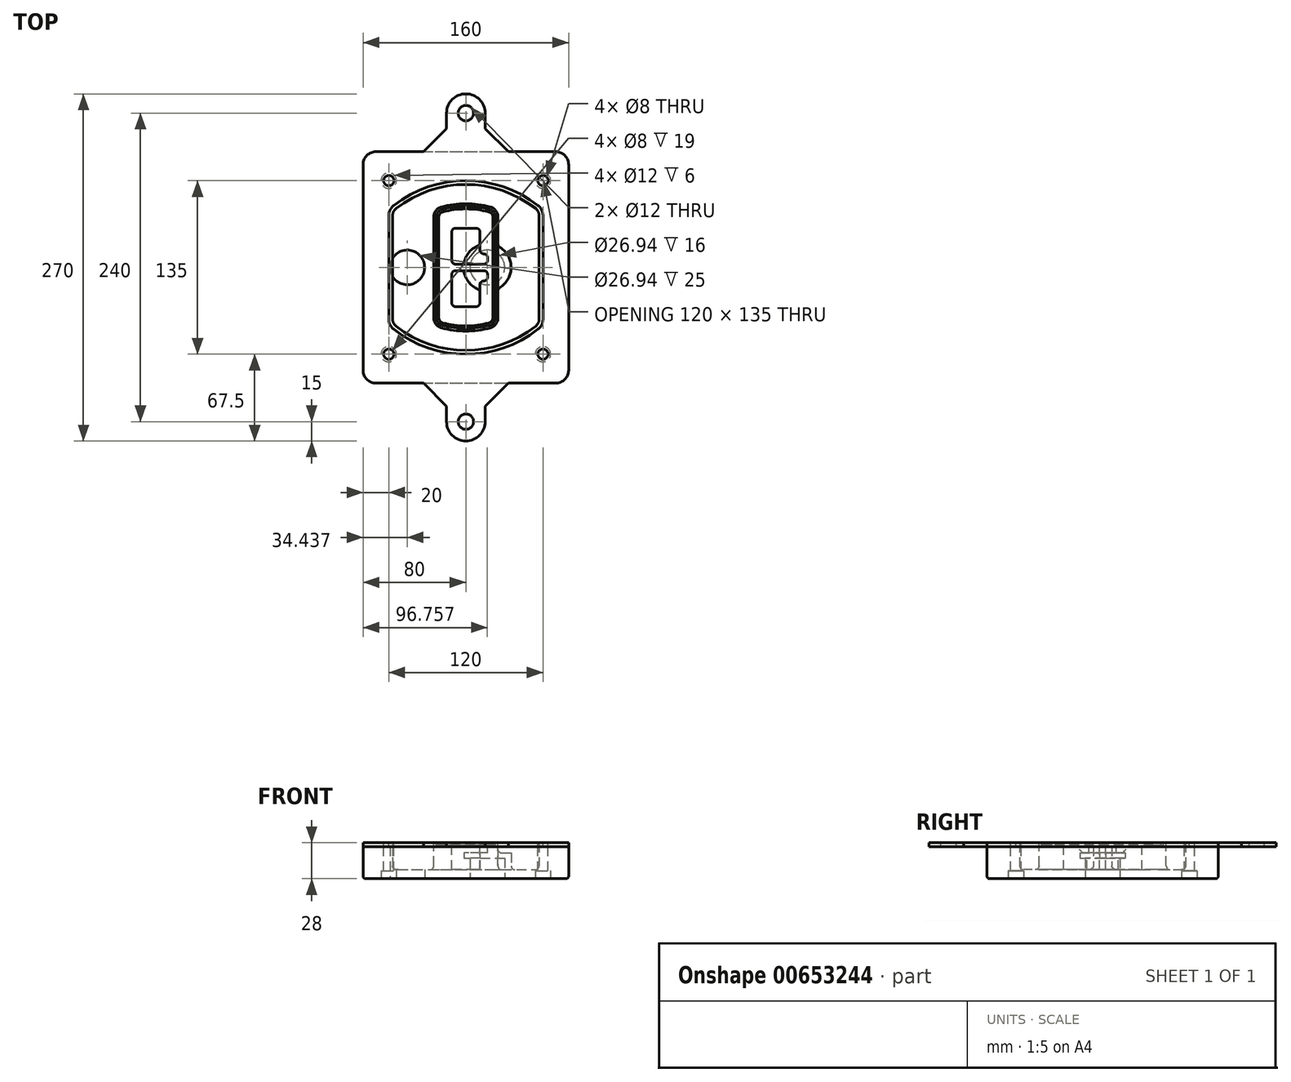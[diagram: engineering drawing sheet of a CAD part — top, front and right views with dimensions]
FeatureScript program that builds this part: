
annotation { "Feature Type Name" : "Feature", "Feature Type Description" : "" }
export const myFeature = defineFeature(function(context is Context, id is Id, definition is map)
    precondition{}
    {
        {
            var Q0;
            Q0=qCreatedBy(makeId("Top.planeOp"),FACE);
            var sketch = newSketch(context, id + "F0", { "sketchPlane" : qUnion([Q0])});
            skPoint(sketch, "E0.rect.middle", {"position": v(0, 0) * mm});
            skLineSegment(sketch, "E1.bottom", {"start": v(-70, -90) * mm, "end": v(70, -90) * mm});
            skLineSegment(sketch, "E1.top", {"start": v(-70, 90) * mm, "end": v(70, 90) * mm});
            skLineSegment(sketch, "E1.left", {"start": v(-80, -80) * mm, "end": v(-80, 80) * mm});
            skLineSegment(sketch, "E1.right", {"start": v(80, -80) * mm, "end": v(80, 80) * mm});
            skLineSegment(sketch, "E2", {"start": v(-80, 90) * mm, "end": v(80, -90) * mm, "construction": true});
            skLineSegment(sketch, "E3", {"start": v(80, 90) * mm, "end": v(-80, -90) * mm, "construction": true});
            skCircle(sketch, "E4", {"center": v(-60, 67.5) * mm, "radius": 4 * mm});
            skCircle(sketch, "E5", {"center": v(60, 67.5) * mm, "radius": 4 * mm});
            skCircle(sketch, "E6", {"center": v(60, -67.5) * mm, "radius": 4 * mm});
            skCircle(sketch, "E7", {"center": v(-60, -67.5) * mm, "radius": 4 * mm});
            skLineSegment(sketch, "E8", {"start": v(-60, 67.5) * mm, "end": v(60, 67.5) * mm, "construction": true});
            skLineSegment(sketch, "E9", {"start": v(60, 67.5) * mm, "end": v(60, -67.5) * mm, "construction": true});
            skLineSegment(sketch, "E10", {"start": v(60, -67.5) * mm, "end": v(-60, -67.5) * mm, "construction": true});
            skLineSegment(sketch, "E11", {"start": v(-60, -67.5) * mm, "end": v(-60, 67.5) * mm, "construction": true});
            skLineSegment(sketch, "E12", {"start": v(-60, 40.3) * mm, "end": v(-60, -40.3) * mm});
            skLineSegment(sketch, "E13", {"start": v(60, 40.3) * mm, "end": v(60, -40.3) * mm});
            skArc(sketch, "E14", {"start": v(56.15, 48.18) * mm, "mid": v(0, 67.5) * mm, "end": v(-56.15, 48.18) * mm});
            skArc(sketch, "E15", {"start": v(-56.15, -48.18) * mm, "mid": v(0, -67.5) * mm, "end": v(56.15, -48.18) * mm});
            skLineSegment(sketch, "E16", {"start": v(-60, 0) * mm, "end": v(60, 0) * mm, "construction": true});
            skPoint(sketch, "E17.visualSharp", {"position": v(-60, -45) * mm});
            skArc(sketch, "E17.filletArc", {"start": v(-60, -40.3) * mm, "mid": v(-58.99, -44.68) * mm, "end": v(-56.15, -48.18) * mm});
            skPoint(sketch, "E18.visualSharp", {"position": v(-60, 45) * mm});
            skArc(sketch, "E18.filletArc", {"start": v(-56.15, 48.18) * mm, "mid": v(-58.99, 44.68) * mm, "end": v(-60, 40.3) * mm});
            skPoint(sketch, "E19.visualSharp", {"position": v(60, 45) * mm});
            skArc(sketch, "E19.filletArc", {"start": v(60, 40.3) * mm, "mid": v(58.99, 44.68) * mm, "end": v(56.15, 48.18) * mm});
            skPoint(sketch, "E20.visualSharp", {"position": v(60, -45) * mm});
            skArc(sketch, "E20.filletArc", {"start": v(56.15, -48.18) * mm, "mid": v(58.99, -44.68) * mm, "end": v(60, -40.3) * mm});
            skPoint(sketch, "E21.visualSharp", {"position": v(-80, 90) * mm});
            skArc(sketch, "E21.filletArc", {"start": v(-70, 90) * mm, "mid": v(-77.07, 87.07) * mm, "end": v(-80, 80) * mm});
            skPoint(sketch, "E22.visualSharp", {"position": v(80, 90) * mm});
            skArc(sketch, "E22.filletArc", {"start": v(80, 80) * mm, "mid": v(77.07, 87.07) * mm, "end": v(70, 90) * mm});
            skPoint(sketch, "E23.visualSharp", {"position": v(80, -90) * mm});
            skArc(sketch, "E23.filletArc", {"start": v(70, -90) * mm, "mid": v(77.07, -87.07) * mm, "end": v(80, -80) * mm});
            skPoint(sketch, "E24.visualSharp", {"position": v(-80, -90) * mm});
            skArc(sketch, "E24.filletArc", {"start": v(-80, -80) * mm, "mid": v(-77.07, -87.07) * mm, "end": v(-70, -90) * mm});
            skArc(sketch, "E25.0", {"start": v(57, 40.3) * mm, "mid": v(56.3, 43.36) * mm, "end": v(54.3, 45.81) * mm});
            skLineSegment(sketch, "E25.1", {"start": v(57, 40.3) * mm, "end": v(57, -40.3) * mm});
            skArc(sketch, "E25.2", {"start": v(54.3, -45.81) * mm, "mid": v(56.3, -43.36) * mm, "end": v(57, -40.3) * mm});
            skArc(sketch, "E25.3", {"start": v(-54.3, -45.81) * mm, "mid": v(0, -64.5) * mm, "end": v(54.3, -45.81) * mm});
            skArc(sketch, "E25.4", {"start": v(-57, -40.3) * mm, "mid": v(-56.3, -43.36) * mm, "end": v(-54.3, -45.81) * mm});
            skArc(sketch, "E25.5", {"start": v(54.3, 45.81) * mm, "mid": v(0, 64.5) * mm, "end": v(-54.3, 45.81) * mm});
            skLineSegment(sketch, "E25.6", {"start": v(-57, 40.3) * mm, "end": v(-57, -40.3) * mm});
            skArc(sketch, "E25.7", {"start": v(-54.3, 45.81) * mm, "mid": v(-56.3, 43.36) * mm, "end": v(-57, 40.3) * mm});
            skArc(sketch, "E26.0", {"start": v(-58.62, 51.33) * mm, "mid": v(-62.58, 46.43) * mm, "end": v(-64, 40.3) * mm});
            skArc(sketch, "E26.1", {"start": v(58.62, 51.33) * mm, "mid": v(0, 71.5) * mm, "end": v(-58.62, 51.33) * mm});
            skArc(sketch, "E26.2", {"start": v(64, 40.3) * mm, "mid": v(62.58, 46.43) * mm, "end": v(58.62, 51.33) * mm});
            skLineSegment(sketch, "E26.3", {"start": v(64, 40.3) * mm, "end": v(64, -40.3) * mm});
            skArc(sketch, "E26.4", {"start": v(58.62, -51.33) * mm, "mid": v(62.58, -46.43) * mm, "end": v(64, -40.3) * mm});
            skLineSegment(sketch, "E26.5", {"start": v(-64, 40.3) * mm, "end": v(-64, -40.3) * mm});
            skArc(sketch, "E26.6", {"start": v(-58.62, -51.33) * mm, "mid": v(0, -71.5) * mm, "end": v(58.62, -51.33) * mm});
            skArc(sketch, "E26.7", {"start": v(-64, -40.3) * mm, "mid": v(-62.58, -46.43) * mm, "end": v(-58.62, -51.33) * mm});
            skSolve(sketch);
        }
        {
            var Q0;
            Q0=makeQuery(id+"F0.imprint","IMPRINT",FACE,{"disambiguationData":[TD([[makeQuery(id+"F0.imprint","IMPRINT",EDGE,{"derivedFrom":sQuery(id+"F0.wireOp",EDGE,"E1.bottom")}),1.0]])]});
            var Q1;
            Q1=makeQuery(id+"F0.imprint","IMPRINT",FACE,{"disambiguationData":[TD([[makeQuery(id+"F0.imprint","IMPRINT",EDGE,{"derivedFrom":sQuery(id+"F0.wireOp",EDGE,"E12")}),1.0]])]});
            var Q2;
            Q2=makeQuery(id+"F0.imprint","IMPRINT",FACE,{"disambiguationData":[TD([[makeQuery(id+"F0.imprint","IMPRINT",EDGE,{"derivedFrom":sQuery(id+"F0.wireOp",EDGE,"E25.0")}),1.0]])]});
            var Q3;
            Q3=makeQuery(id+"F0.imprint","IMPRINT",FACE,{"disambiguationData":[TD([[makeQuery(id+"F0.imprint","IMPRINT",EDGE,{"derivedFrom":sQuery(id+"F0.wireOp",EDGE,"E12")}),-1.0]])]});
            extrude(context, id + "F1", {"entities" : qUnion([Q0, Q1, Q2, Q3]), "oppositeDirection" : true, "depth" : 25 * mm});
        }
        {
            var Q0;
            Q0=makeQuery(id+"F0.imprint","IMPRINT",FACE,{"disambiguationData":[TD([[makeQuery(id+"F0.imprint","IMPRINT",EDGE,{"derivedFrom":sQuery(id+"F0.wireOp",EDGE,"E12")}),1.0]])]});
            extrude(context, id + "F2", {"entities" : qUnion([Q0]), "operationType" : NewBodyOperationType.ADD, "depth" : 3 * mm});
        }
        {
            var Q0;
            Q0=makeQuery(id+"F0.imprint","IMPRINT",FACE,{"disambiguationData":[TD([[makeQuery(id+"F0.imprint","IMPRINT",EDGE,{"derivedFrom":sQuery(id+"F0.wireOp",EDGE,"E25.0")}),1.0]])]});
            extrude(context, id + "F3", {"entities" : qUnion([Q0]), "operationType" : NewBodyOperationType.REMOVE, "oppositeDirection" : true, "depth" : 18 * mm});
        }
        {
            var Q0;
            Q0=makeQuery(id+"F2.opExtrude","CAP_FACE",FACE,{"disambiguationData":[OSD([sQuery(id+"F0.wireOp",EDGE,"E12"),sQuery(id+"F0.wireOp",EDGE,"E13"),sQuery(id+"F0.wireOp",EDGE,"E14"),sQuery(id+"F0.wireOp",EDGE,"E15"),sQuery(id+"F0.wireOp",EDGE,"E17.filletArc"),sQuery(id+"F0.wireOp",EDGE,"E18.filletArc"),sQuery(id+"F0.wireOp",EDGE,"E19.filletArc"),sQuery(id+"F0.wireOp",EDGE,"E20.filletArc"),sQuery(id+"F0.wireOp",EDGE,"E25.0"),sQuery(id+"F0.wireOp",EDGE,"E25.1"),sQuery(id+"F0.wireOp",EDGE,"E25.2"),sQuery(id+"F0.wireOp",EDGE,"E25.3"),sQuery(id+"F0.wireOp",EDGE,"E25.4"),sQuery(id+"F0.wireOp",EDGE,"E25.5"),sQuery(id+"F0.wireOp",EDGE,"E25.6"),sQuery(id+"F0.wireOp",EDGE,"E25.7")])],"isStart":false});
            var sketch = newSketch(context, id + "F4", { "sketchPlane" : qUnion([Q0])});
            skArc(sketch, "E27.0", {"start": v(-19.08, -46.97) * mm, "mid": v(0, -49.5) * mm, "end": v(19.08, -46.97) * mm});
            skArc(sketch, "E28.0", {"start": v(19.08, 46.97) * mm, "mid": v(0, 49.5) * mm, "end": v(-19.08, 46.97) * mm});
            skLineSegment(sketch, "E29", {"start": v(-25, 39.25) * mm, "end": v(-25, -39.25) * mm});
            skLineSegment(sketch, "E30", {"start": v(25, 39.25) * mm, "end": v(25, -39.25) * mm});
            skLineSegment(sketch, "E31", {"start": v(-25, 45.1) * mm, "end": v(25, 45.1) * mm, "construction": true});
            skLineSegment(sketch, "E32", {"start": v(-25, -45.1) * mm, "end": v(25, -45.1) * mm, "construction": true});
            skPoint(sketch, "E33.visualSharp", {"position": v(-25, 45.1) * mm});
            skArc(sketch, "E33.filletArc", {"start": v(-19.08, 46.97) * mm, "mid": v(-23.35, 44.11) * mm, "end": v(-25, 39.25) * mm});
            skPoint(sketch, "E34.visualSharp", {"position": v(25, 45.1) * mm});
            skArc(sketch, "E34.filletArc", {"start": v(25, 39.25) * mm, "mid": v(23.35, 44.11) * mm, "end": v(19.08, 46.97) * mm});
            skPoint(sketch, "E35.visualSharp", {"position": v(25, -45.1) * mm});
            skArc(sketch, "E35.filletArc", {"start": v(19.08, -46.97) * mm, "mid": v(23.35, -44.11) * mm, "end": v(25, -39.25) * mm});
            skPoint(sketch, "E36.visualSharp", {"position": v(-25, -45.1) * mm});
            skArc(sketch, "E36.filletArc", {"start": v(-25, -39.25) * mm, "mid": v(-23.35, -44.11) * mm, "end": v(-19.08, -46.97) * mm});
            skArc(sketch, "E37.0", {"start": v(54.3, 45.81) * mm, "mid": v(0, 64.5) * mm, "end": v(-54.3, 45.81) * mm});
            skArc(sketch, "E37.1", {"start": v(-54.3, 45.81) * mm, "mid": v(-56.3, 43.36) * mm, "end": v(-57, 40.3) * mm});
            skLineSegment(sketch, "E37.2", {"start": v(-57, 40.3) * mm, "end": v(-57, -40.3) * mm});
            skArc(sketch, "E37.3", {"start": v(-57, -40.3) * mm, "mid": v(-56.3, -43.36) * mm, "end": v(-54.3, -45.81) * mm});
            skArc(sketch, "E37.4", {"start": v(-54.3, -45.81) * mm, "mid": v(0, -64.5) * mm, "end": v(54.3, -45.81) * mm});
            skArc(sketch, "E37.5", {"start": v(54.3, -45.81) * mm, "mid": v(56.3, -43.36) * mm, "end": v(57, -40.3) * mm});
            skLineSegment(sketch, "E37.6", {"start": v(57, 40.3) * mm, "end": v(57, -40.3) * mm});
            skArc(sketch, "E37.7", {"start": v(57, 40.3) * mm, "mid": v(56.3, 43.36) * mm, "end": v(54.3, 45.81) * mm});
            skLineSegment(sketch, "E38.0", {"start": v(23, 39.25) * mm, "end": v(23, -39.25) * mm});
            skArc(sketch, "E38.1", {"start": v(18.56, -45.04) * mm, "mid": v(21.76, -42.9) * mm, "end": v(23, -39.25) * mm});
            skArc(sketch, "E38.2", {"start": v(-18.56, -45.04) * mm, "mid": v(0, -47.5) * mm, "end": v(18.56, -45.04) * mm});
            skArc(sketch, "E38.3", {"start": v(-23, -39.25) * mm, "mid": v(-21.76, -42.9) * mm, "end": v(-18.56, -45.04) * mm});
            skLineSegment(sketch, "E38.4", {"start": v(-23, 39.25) * mm, "end": v(-23, -39.25) * mm});
            skArc(sketch, "E38.5", {"start": v(23, 39.25) * mm, "mid": v(21.76, 42.9) * mm, "end": v(18.56, 45.04) * mm});
            skArc(sketch, "E38.6", {"start": v(-18.56, 45.04) * mm, "mid": v(-21.76, 42.9) * mm, "end": v(-23, 39.25) * mm});
            skArc(sketch, "E38.7", {"start": v(18.56, 45.04) * mm, "mid": v(0, 47.5) * mm, "end": v(-18.56, 45.04) * mm});
            skArc(sketch, "E39.0", {"start": v(21, 39.25) * mm, "mid": v(20.18, 41.68) * mm, "end": v(18.04, 43.1) * mm});
            skLineSegment(sketch, "E39.1", {"start": v(21, 39.25) * mm, "end": v(21, -39.25) * mm});
            skArc(sketch, "E39.2", {"start": v(18.04, -43.1) * mm, "mid": v(20.18, -41.68) * mm, "end": v(21, -39.25) * mm});
            skArc(sketch, "E39.3", {"start": v(-18.04, -43.1) * mm, "mid": v(0, -45.5) * mm, "end": v(18.04, -43.1) * mm});
            skArc(sketch, "E39.4", {"start": v(-21, -39.25) * mm, "mid": v(-20.18, -41.68) * mm, "end": v(-18.04, -43.1) * mm});
            skArc(sketch, "E39.5", {"start": v(18.04, 43.1) * mm, "mid": v(0, 45.5) * mm, "end": v(-18.04, 43.1) * mm});
            skLineSegment(sketch, "E39.6", {"start": v(-21, 39.25) * mm, "end": v(-21, -39.25) * mm});
            skArc(sketch, "E39.7", {"start": v(-18.04, 43.1) * mm, "mid": v(-20.18, 41.68) * mm, "end": v(-21, 39.25) * mm});
            skLineSegment(sketch, "E40", {"start": v(-25, 0) * mm, "end": v(25, 0) * mm, "construction": true});
            skLineSegment(sketch, "E41", {"start": v(-11, 5.5) * mm, "end": v(-11, 27.5) * mm});
            skLineSegment(sketch, "E42", {"start": v(-8, 30.5) * mm, "end": v(8, 30.5) * mm});
            skLineSegment(sketch, "E43", {"start": v(11, 27.5) * mm, "end": v(11, 13.5) * mm});
            skLineSegment(sketch, "E44", {"start": v(14, 10.5) * mm, "end": v(14, 10.5) * mm});
            skLineSegment(sketch, "E45", {"start": v(17, 7.5) * mm, "end": v(17, 5.5) * mm});
            skLineSegment(sketch, "E46", {"start": v(14, 2.5) * mm, "end": v(-8, 2.5) * mm});
            skPoint(sketch, "E47.visualSharp", {"position": v(-11, 30.5) * mm});
            skArc(sketch, "E47.filletArc", {"start": v(-8, 30.5) * mm, "mid": v(-10.12, 29.62) * mm, "end": v(-11, 27.5) * mm});
            skPoint(sketch, "E48.visualSharp", {"position": v(11, 30.5) * mm});
            skArc(sketch, "E48.filletArc", {"start": v(11, 27.5) * mm, "mid": v(10.12, 29.62) * mm, "end": v(8, 30.5) * mm});
            skPoint(sketch, "E49.visualSharp", {"position": v(11, 10.5) * mm});
            skArc(sketch, "E49.filletArc", {"start": v(11, 13.5) * mm, "mid": v(11.88, 11.38) * mm, "end": v(14, 10.5) * mm});
            skPoint(sketch, "E50.visualSharp", {"position": v(17, 10.5) * mm});
            skArc(sketch, "E50.filletArc", {"start": v(17, 7.5) * mm, "mid": v(16.12, 9.62) * mm, "end": v(14, 10.5) * mm});
            skPoint(sketch, "E51.visualSharp", {"position": v(17, 2.5) * mm});
            skArc(sketch, "E51.filletArc", {"start": v(14, 2.5) * mm, "mid": v(16.12, 3.38) * mm, "end": v(17, 5.5) * mm});
            skPoint(sketch, "E52.visualSharp", {"position": v(-11, 2.5) * mm});
            skArc(sketch, "E52.filletArc", {"start": v(-11, 5.5) * mm, "mid": v(-10.12, 3.38) * mm, "end": v(-8, 2.5) * mm});
            skLineSegment(sketch, "E53.0.MirrorCS", {"start": v(14, -2.5) * mm, "end": v(-8, -2.5) * mm});
            skArc(sketch, "E54.0.MirrorCS", {"start": v(-11, -5.5) * mm, "mid": v(-10.12, -3.38) * mm, "end": v(-8, -2.5) * mm});
            skLineSegment(sketch, "E55.0.MirrorCS", {"start": v(-11, -5.5) * mm, "end": v(-11, -27.5) * mm});
            skArc(sketch, "E56.0.MirrorCS", {"start": v(-8, -30.5) * mm, "mid": v(-10.12, -29.62) * mm, "end": v(-11, -27.5) * mm});
            skLineSegment(sketch, "E57.0.MirrorCS", {"start": v(-8, -30.5) * mm, "end": v(8, -30.5) * mm});
            skArc(sketch, "E58.0.MirrorCS", {"start": v(11, -27.5) * mm, "mid": v(10.12, -29.62) * mm, "end": v(8, -30.5) * mm});
            skLineSegment(sketch, "E59.0.MirrorCS", {"start": v(11, -27.5) * mm, "end": v(11, -13.5) * mm});
            skArc(sketch, "E60.0.MirrorCS", {"start": v(11, -13.5) * mm, "mid": v(11.88, -11.38) * mm, "end": v(14, -10.5) * mm});
            skArc(sketch, "E61.0.MirrorCS", {"start": v(17, -7.5) * mm, "mid": v(16.12, -9.62) * mm, "end": v(14, -10.5) * mm});
            skLineSegment(sketch, "E62.0.MirrorCS", {"start": v(17, -7.5) * mm, "end": v(17, -5.5) * mm});
            skArc(sketch, "E63.0.MirrorCS", {"start": v(14, -2.5) * mm, "mid": v(16.12, -3.38) * mm, "end": v(17, -5.5) * mm});
            skSolve(sketch);
        }
        {
            var Q0;
            Q0=makeQuery(id+"F4.imprint","IMPRINT",FACE,{"disambiguationData":[TD([[makeQuery(id+"F4.imprint","IMPRINT",EDGE,{"derivedFrom":sQuery(id+"F4.wireOp",EDGE,"E27.0")}),1.0]])]});
            var Q1;
            Q1=makeQuery(id+"F4.imprint","IMPRINT",FACE,{"disambiguationData":[TD([[makeQuery(id+"F4.imprint","IMPRINT",EDGE,{"derivedFrom":sQuery(id+"F4.wireOp",EDGE,"E38.0")}),-1.0]])]});
            var Q2;
            Q2=makeQuery(id+"F4.imprint","IMPRINT",FACE,{"disambiguationData":[TD([[makeQuery(id+"F4.imprint","IMPRINT",EDGE,{"derivedFrom":sQuery(id+"F4.wireOp",EDGE,"E39.0")}),1.0]])]});
            extrude(context, id + "F5", {"entities" : qUnion([Q0, Q1, Q2]), "operationType" : NewBodyOperationType.ADD, "endBound" : BoundingType.UP_TO_NEXT, "oppositeDirection" : true, "depth" : 25 * mm});
        }
        {
            var Q0;
            Q0=makeQuery(id+"F4.imprint","IMPRINT",FACE,{"disambiguationData":[TD([[makeQuery(id+"F4.imprint","IMPRINT",EDGE,{"derivedFrom":sQuery(id+"F4.wireOp",EDGE,"E38.0")}),-1.0]])]});
            extrude(context, id + "F6", {"entities" : qUnion([Q0]), "operationType" : NewBodyOperationType.REMOVE, "oppositeDirection" : true, "depth" : 2 * mm});
        }
        {
            var Q0;
            Q0=makeQuery(id+"F1.opExtrude","CAP_FACE",FACE,{"disambiguationData":[OSD([sQuery(id+"F0.wireOp",EDGE,"E1.bottom"),sQuery(id+"F0.wireOp",EDGE,"E1.top"),sQuery(id+"F0.wireOp",EDGE,"E1.left"),sQuery(id+"F0.wireOp",EDGE,"E1.right"),sQuery(id+"F0.wireOp",EDGE,"E4"),sQuery(id+"F0.wireOp",EDGE,"E5"),sQuery(id+"F0.wireOp",EDGE,"E6"),sQuery(id+"F0.wireOp",EDGE,"E7"),sQuery(id+"F0.wireOp",EDGE,"E21.filletArc"),sQuery(id+"F0.wireOp",EDGE,"E22.filletArc"),sQuery(id+"F0.wireOp",EDGE,"E23.filletArc"),sQuery(id+"F0.wireOp",EDGE,"E24.filletArc")])],"isStart":false});
            var sketch = newSketch(context, id + "F7", { "sketchPlane" : qUnion([Q0])});
            skCircle(sketch, "E64", {"center": v(16.76, 0) * mm, "radius": 13.47 * mm});
            skCircle(sketch, "E65", {"center": v(-45.56, 0) * mm, "radius": 13.47 * mm});
            skLineSegment(sketch, "E66", {"start": v(80, 0) * mm, "end": v(-80, 0) * mm});
            skCircle(sketch, "E67", {"center": v(16.76, 0) * mm, "radius": 18.47 * mm});
            skCircle(sketch, "E68", {"center": v(60, -67.5) * mm, "radius": 6 * mm});
            skCircle(sketch, "E69", {"center": v(-60, -67.5) * mm, "radius": 6 * mm});
            skCircle(sketch, "E70", {"center": v(-60, 67.5) * mm, "radius": 6 * mm});
            skCircle(sketch, "E71", {"center": v(60, 67.5) * mm, "radius": 6 * mm});
            skSolve(sketch);
        }
        {
            var Q0;
            {var subQ1=sQuery(id+"F7.wireOp",EDGE,"E66");var subQ4=sQuery(id+"F7.wireOp",EDGE,"E64");var subQ6=makeQuery(id+"F7.imprint","INTERSECT",VERTEX,{"disambiguationData":[OD(0.0)],"derivedFrom":[subQ4,subQ1]});Q0=makeQuery(id+"F7.imprint","IMPRINT",FACE,{"disambiguationData":[TD([[makeQuery(id+"F7.imprint","IMPRINT",EDGE,{"disambiguationData":[TD([[subQ6,-1.0]])],"derivedFrom":subQ4}),-1.0]])]});}
            var Q1;
            {var subQ0=sQuery(id+"F7.wireOp",EDGE,"E66");var subQ1=sQuery(id+"F7.wireOp",EDGE,"E64");var subQ3=makeQuery(id+"F7.imprint","INTERSECT",VERTEX,{"disambiguationData":[OD(0.0)],"derivedFrom":[subQ1,subQ0]});Q1=makeQuery(id+"F7.imprint","IMPRINT",FACE,{"disambiguationData":[TD([[makeQuery(id+"F7.imprint","IMPRINT",EDGE,{"disambiguationData":[TD([[subQ3,-1.0]])],"derivedFrom":subQ1}),1.0]])]});}
            var Q2;
            {var subQ0=sQuery(id+"F7.wireOp",EDGE,"E66");var subQ1=sQuery(id+"F7.wireOp",EDGE,"E64");var subQ3=makeQuery(id+"F7.imprint","INTERSECT",VERTEX,{"disambiguationData":[OD(0.0)],"derivedFrom":[subQ1,subQ0]});Q2=makeQuery(id+"F7.imprint","IMPRINT",FACE,{"disambiguationData":[TD([[makeQuery(id+"F7.imprint","IMPRINT",EDGE,{"disambiguationData":[TD([[subQ3,1.0]])],"derivedFrom":subQ1}),1.0]])]});}
            var Q3;
            {var subQ1=sQuery(id+"F7.wireOp",EDGE,"E66");var subQ4=sQuery(id+"F7.wireOp",EDGE,"E64");var subQ6=makeQuery(id+"F7.imprint","INTERSECT",VERTEX,{"disambiguationData":[OD(0.0)],"derivedFrom":[subQ4,subQ1]});Q3=makeQuery(id+"F7.imprint","IMPRINT",FACE,{"disambiguationData":[TD([[makeQuery(id+"F7.imprint","IMPRINT",EDGE,{"disambiguationData":[TD([[subQ6,1.0]])],"derivedFrom":subQ4}),-1.0]])]});}
            extrude(context, id + "F8", {"entities" : qUnion([Q0, Q1, Q2, Q3]), "operationType" : NewBodyOperationType.ADD, "oppositeDirection" : true, "depth" : 20 * mm});
        }
        {
            var Q0;
            {var subQ0=sQuery(id+"F7.wireOp",EDGE,"E66");var subQ1=sQuery(id+"F7.wireOp",EDGE,"E64");var subQ3=makeQuery(id+"F7.imprint","INTERSECT",VERTEX,{"disambiguationData":[OD(0.0)],"derivedFrom":[subQ1,subQ0]});Q0=makeQuery(id+"F7.imprint","IMPRINT",FACE,{"disambiguationData":[TD([[makeQuery(id+"F7.imprint","IMPRINT",EDGE,{"disambiguationData":[TD([[subQ3,-1.0]])],"derivedFrom":subQ1}),1.0]])]});}
            var Q1;
            {var subQ0=sQuery(id+"F7.wireOp",EDGE,"E66");var subQ1=sQuery(id+"F7.wireOp",EDGE,"E64");var subQ3=makeQuery(id+"F7.imprint","INTERSECT",VERTEX,{"disambiguationData":[OD(0.0)],"derivedFrom":[subQ1,subQ0]});Q1=makeQuery(id+"F7.imprint","IMPRINT",FACE,{"disambiguationData":[TD([[makeQuery(id+"F7.imprint","IMPRINT",EDGE,{"disambiguationData":[TD([[subQ3,1.0]])],"derivedFrom":subQ1}),1.0]])]});}
            extrude(context, id + "F9", {"entities" : qUnion([Q0, Q1]), "operationType" : NewBodyOperationType.REMOVE, "oppositeDirection" : true, "depth" : 16 * mm});
        }
        {
            var Q0;
            {var subQ0=sQuery(id+"F7.wireOp",EDGE,"E66");var subQ1=sQuery(id+"F7.wireOp",EDGE,"E65");var subQ3=makeQuery(id+"F7.imprint","INTERSECT",VERTEX,{"disambiguationData":[OD(0.0)],"derivedFrom":[subQ1,subQ0]});Q0=makeQuery(id+"F7.imprint","IMPRINT",FACE,{"disambiguationData":[TD([[makeQuery(id+"F7.imprint","IMPRINT",EDGE,{"disambiguationData":[TD([[subQ3,-1.0]])],"derivedFrom":subQ1}),1.0]])]});}
            var Q1;
            {var subQ0=sQuery(id+"F7.wireOp",EDGE,"E66");var subQ1=sQuery(id+"F7.wireOp",EDGE,"E65");var subQ3=makeQuery(id+"F7.imprint","INTERSECT",VERTEX,{"disambiguationData":[OD(0.0)],"derivedFrom":[subQ1,subQ0]});Q1=makeQuery(id+"F7.imprint","IMPRINT",FACE,{"disambiguationData":[TD([[makeQuery(id+"F7.imprint","IMPRINT",EDGE,{"disambiguationData":[TD([[subQ3,1.0]])],"derivedFrom":subQ1}),1.0]])]});}
            extrude(context, id + "F10", {"entities" : qUnion([Q0, Q1]), "operationType" : NewBodyOperationType.REMOVE, "oppositeDirection" : true, "depth" : 25 * mm});
        }
        {
            var Q0;
            Q0=makeQuery(id+"F7.imprint","IMPRINT",FACE,{"disambiguationData":[TD([[makeQuery(id+"F7.imprint","IMPRINT",EDGE,{"derivedFrom":sQuery(id+"F7.wireOp",EDGE,"E68")}),1.0]])]});
            var Q1;
            Q1=makeQuery(id+"F7.imprint","IMPRINT",FACE,{"disambiguationData":[TD([[makeQuery(id+"F7.imprint","IMPRINT",EDGE,{"derivedFrom":makeQuery(id+"F1.opExtrude","CAP_EDGE",EDGE,{"disambiguationData":[OSD([sQuery(id+"F0.wireOp",EDGE,"E5")])],"isStart":false})}),-1.0]])]});
            var Q2;
            Q2=makeQuery(id+"F7.imprint","IMPRINT",FACE,{"disambiguationData":[TD([[makeQuery(id+"F7.imprint","IMPRINT",EDGE,{"derivedFrom":sQuery(id+"F7.wireOp",EDGE,"E69")}),1.0]])]});
            var Q3;
            Q3=makeQuery(id+"F7.imprint","IMPRINT",FACE,{"disambiguationData":[TD([[makeQuery(id+"F7.imprint","IMPRINT",EDGE,{"derivedFrom":makeQuery(id+"F1.opExtrude","CAP_EDGE",EDGE,{"disambiguationData":[OSD([sQuery(id+"F0.wireOp",EDGE,"E4")])],"isStart":false})}),-1.0]])]});
            var Q4;
            Q4=makeQuery(id+"F7.imprint","IMPRINT",FACE,{"disambiguationData":[TD([[makeQuery(id+"F7.imprint","IMPRINT",EDGE,{"derivedFrom":sQuery(id+"F7.wireOp",EDGE,"E70")}),1.0]])]});
            var Q5;
            Q5=makeQuery(id+"F7.imprint","IMPRINT",FACE,{"disambiguationData":[TD([[makeQuery(id+"F7.imprint","IMPRINT",EDGE,{"derivedFrom":makeQuery(id+"F1.opExtrude","CAP_EDGE",EDGE,{"disambiguationData":[OSD([sQuery(id+"F0.wireOp",EDGE,"E7")])],"isStart":false})}),-1.0]])]});
            var Q6;
            Q6=makeQuery(id+"F7.imprint","IMPRINT",FACE,{"disambiguationData":[TD([[makeQuery(id+"F7.imprint","IMPRINT",EDGE,{"derivedFrom":sQuery(id+"F7.wireOp",EDGE,"E71")}),1.0]])]});
            var Q7;
            Q7=makeQuery(id+"F7.imprint","IMPRINT",FACE,{"disambiguationData":[TD([[makeQuery(id+"F7.imprint","IMPRINT",EDGE,{"derivedFrom":makeQuery(id+"F1.opExtrude","CAP_EDGE",EDGE,{"disambiguationData":[OSD([sQuery(id+"F0.wireOp",EDGE,"E6")])],"isStart":false})}),-1.0]])]});
            extrude(context, id + "F11", {"entities" : qUnion([Q0, Q1, Q2, Q3, Q4, Q5, Q6, Q7]), "operationType" : NewBodyOperationType.REMOVE, "oppositeDirection" : true, "depth" : 6 * mm});
        }
        {
            var Q0;
            Q0=makeQuery(id+"F9.boolean.opBoolean","COPY",FACE,{"derivedFrom":makeQuery(id+"F9.opExtrude","CAP_FACE",FACE,{"disambiguationData":[OSD([sQuery(id+"F7.wireOp",EDGE,"E64")])],"isStart":false})});
            var sketch = newSketch(context, id + "F12", { "sketchPlane" : qUnion([Q0])});
            skArc(sketch, "E72.0", {"start": v(11, 17.55) * mm, "mid": v(2.57, 11.82) * mm, "end": v(-1.54, 2.5) * mm});
            skArc(sketch, "E72.1", {"start": v(-1.54, -2.5) * mm, "mid": v(2.57, -11.82) * mm, "end": v(11, -17.55) * mm});
            skLineSegment(sketch, "E73", {"start": v(-1.54, -2.5) * mm, "end": v(14, -2.5) * mm});
            skLineSegment(sketch, "E74.0", {"start": v(14, 2.5) * mm, "end": v(-1.54, 2.5) * mm});
            skArc(sketch, "E74.1", {"start": v(14, 2.5) * mm, "mid": v(16.12, 3.38) * mm, "end": v(17, 5.5) * mm});
            skLineSegment(sketch, "E74.2", {"start": v(17, 7.5) * mm, "end": v(17, 5.5) * mm});
            skArc(sketch, "E74.3", {"start": v(17, 7.5) * mm, "mid": v(16.12, 9.62) * mm, "end": v(14, 10.5) * mm});
            skArc(sketch, "E74.4", {"start": v(11, 13.5) * mm, "mid": v(11.88, 11.38) * mm, "end": v(14, 10.5) * mm});
            skLineSegment(sketch, "E74.5", {"start": v(11, 17.55) * mm, "end": v(11, 13.5) * mm});
            skLineSegment(sketch, "E74.7", {"start": v(14, -2.5) * mm, "end": v(-1.54, -2.5) * mm});
            skArc(sketch, "E74.8", {"start": v(14, -2.5) * mm, "mid": v(16.12, -3.38) * mm, "end": v(17, -5.5) * mm});
            skLineSegment(sketch, "E74.9", {"start": v(17, -7.5) * mm, "end": v(17, -5.5) * mm});
            skArc(sketch, "E74.10", {"start": v(17, -7.5) * mm, "mid": v(16.12, -9.62) * mm, "end": v(14, -10.5) * mm});
            skArc(sketch, "E74.11", {"start": v(11, -13.5) * mm, "mid": v(11.88, -11.38) * mm, "end": v(14, -10.5) * mm});
            skLineSegment(sketch, "E74.12", {"start": v(11, -17.55) * mm, "end": v(11, -13.5) * mm});
            skPoint(sketch, "E75.orphan", {"position": v(11, -27.5) * mm});
            skPoint(sketch, "E76.orphan", {"position": v(-8, -2.5) * mm});
            skPoint(sketch, "E77.orphan", {"position": v(-8, 2.5) * mm});
            skPoint(sketch, "E78.orphan", {"position": v(11, 27.5) * mm});
            skSolve(sketch);
        }
        {
            var Q0;
            {var subQ7=sQuery(id+"F12.wireOp",EDGE,"E72.0");var subQ14=sQuery(id+"F12.wireOp",EDGE,"E72.1");var subQ16=sQuery(id+"F12.wireOp",EDGE,"E74.1");var subQ18=sQuery(id+"F12.wireOp",EDGE,"E74.8");Q0=qUnion([makeQuery(id+"F12.imprint","IMPRINT",FACE,{"disambiguationData":[TD([[makeQuery(id+"F12.imprint","IMPRINT",EDGE,{"derivedFrom":subQ7}),1.0]])]}),makeQuery(id+"F12.imprint","IMPRINT",FACE,{"disambiguationData":[TD([[makeQuery(id+"F12.imprint","IMPRINT",EDGE,{"derivedFrom":subQ14}),1.0]])]}),makeQuery(id+"F12.imprint","IMPRINT",FACE,{"disambiguationData":[TD([[makeQuery(id+"F12.imprint","IMPRINT",EDGE,{"derivedFrom":subQ16}),1.0]])]}),makeQuery(id+"F12.imprint","IMPRINT",FACE,{"disambiguationData":[TD([[makeQuery(id+"F12.imprint","IMPRINT",EDGE,{"derivedFrom":subQ18}),-1.0]])]})]);}
            var Q1;
            Q1=makeQuery(id+"F5.boolean.opBoolean","SPLIT",FACE,{"disambiguationData":[TD([makeQuery(id+"F5.opExtrude","SWEPT_FACE",FACE,{"disambiguationData":[OSD([sQuery(id+"F4.wireOp",EDGE,"E41")])]})])],"derivedFrom":makeQuery(id+"F3.boolean.opBoolean","COPY",FACE,{"derivedFrom":makeQuery(id+"F3.opExtrude","CAP_FACE",FACE,{"disambiguationData":[OSD([sQuery(id+"F0.wireOp",EDGE,"E25.0"),sQuery(id+"F0.wireOp",EDGE,"E25.1"),sQuery(id+"F0.wireOp",EDGE,"E25.2"),sQuery(id+"F0.wireOp",EDGE,"E25.3"),sQuery(id+"F0.wireOp",EDGE,"E25.4"),sQuery(id+"F0.wireOp",EDGE,"E25.5"),sQuery(id+"F0.wireOp",EDGE,"E25.6"),sQuery(id+"F0.wireOp",EDGE,"E25.7")])],"isStart":false})})});
            extrude(context, id + "F13", {"entities" : qUnion([Q0]), "operationType" : NewBodyOperationType.REMOVE, "endBound" : BoundingType.UP_TO_SURFACE, "endBoundEntityFace" : qUnion([Q1]), "depth" : 25 * mm});
        }
        {
            var Q0;
            Q0=makeQuery(id+"F3.boolean.opBoolean","COPY",EDGE,{"derivedFrom":makeQuery(id+"F3.opExtrude","CAP_EDGE",EDGE,{"disambiguationData":[OSD([sQuery(id+"F0.wireOp",EDGE,"E25.6")])],"isStart":false})});
            var Q1;
            Q1=makeQuery(id+"F8.boolean.opBoolean","INTERSECT",EDGE,{"derivedFrom":[makeQuery(id+"F5.opExtrude","SWEPT_FACE",FACE,{"disambiguationData":[OSD([sQuery(id+"F4.wireOp",EDGE,"E30")])]}),makeQuery(id+"F8.opExtrude","CAP_FACE",FACE,{"disambiguationData":[OSD([sQuery(id+"F7.wireOp",EDGE,"E67")])],"isStart":false})]});
            var Q2;
            Q2=makeQuery(id+"F8.boolean.opBoolean","INTERSECT",EDGE,{"disambiguationData":[OD(1.0)],"derivedFrom":[makeQuery(id+"F5.opExtrude","SWEPT_FACE",FACE,{"disambiguationData":[OSD([sQuery(id+"F4.wireOp",EDGE,"E30")])]}),makeQuery(id+"F8.opExtrude","SWEPT_FACE",FACE,{"disambiguationData":[OSD([sQuery(id+"F7.wireOp",EDGE,"E67")])]})]});
            var Q3;
            {var subQ0=sQuery(id+"F4.wireOp",EDGE,"E30");Q3=makeQuery(id+"F8.boolean.opBoolean","SPLIT",EDGE,{"disambiguationData":[TD([makeQuery(id+"F5.opExtrude","SWEPT_FACE",FACE,{"disambiguationData":[OSD([sQuery(id+"F4.wireOp",EDGE,"E35.filletArc")])]})])],"derivedFrom":makeQuery(id+"F5.opExtrude","CAP_EDGE",EDGE,{"disambiguationData":[OSD([subQ0])],"isStart":false})});}
            var Q4;
            {var subQ0=sQuery(id+"F0.wireOp",EDGE,"E25.7");var subQ1=sQuery(id+"F0.wireOp",EDGE,"E25.1");var subQ2=sQuery(id+"F0.wireOp",EDGE,"E25.6");var subQ3=sQuery(id+"F0.wireOp",EDGE,"E25.5");var subQ4=sQuery(id+"F0.wireOp",EDGE,"E25.4");var subQ5=sQuery(id+"F0.wireOp",EDGE,"E25.0");var subQ6=sQuery(id+"F0.wireOp",EDGE,"E25.2");var subQ7=sQuery(id+"F0.wireOp",EDGE,"E25.3");Q4=makeQuery(id+"F8.boolean.opBoolean","INTERSECT",EDGE,{"derivedFrom":[makeQuery(id+"F5.boolean.opBoolean","SPLIT",FACE,{"disambiguationData":[TD([makeQuery(id+"F2.opExtrude","SWEPT_FACE",FACE,{"disambiguationData":[OSD([subQ5])]})])],"derivedFrom":makeQuery(id+"F3.boolean.opBoolean","COPY",FACE,{"derivedFrom":makeQuery(id+"F3.opExtrude","CAP_FACE",FACE,{"disambiguationData":[OSD([subQ5,subQ1,subQ6,subQ7,subQ4,subQ3,subQ2,subQ0])],"isStart":false})})}),makeQuery(id+"F8.opExtrude","SWEPT_FACE",FACE,{"disambiguationData":[OSD([sQuery(id+"F7.wireOp",EDGE,"E67")])]})]});}
            var Q5;
            Q5=makeQuery(id+"F8.boolean.opBoolean","INTERSECT",EDGE,{"disambiguationData":[OD(0.0)],"derivedFrom":[makeQuery(id+"F5.opExtrude","SWEPT_FACE",FACE,{"disambiguationData":[OSD([sQuery(id+"F4.wireOp",EDGE,"E30")])]}),makeQuery(id+"F8.opExtrude","SWEPT_FACE",FACE,{"disambiguationData":[OSD([sQuery(id+"F7.wireOp",EDGE,"E67")])]})]});
            fillet(context, id + "F14", {"entities" : qUnion([Q0, Q1, Q2, Q3, Q4, Q5]), "radius" : 3 * mm, "tangentPropagation" : true, "allowEdgeOverflow" : false});
        }
        {
            var Q0;
            Q0=makeQuery(id+"F1.opExtrude","CAP_EDGE",EDGE,{"disambiguationData":[OSD([sQuery(id+"F0.wireOp",EDGE,"E1.bottom")])],"isStart":false});
            fillet(context, id + "F15", {"entities" : qUnion([Q0]), "radius" : 2 * mm, "tangentPropagation" : true, "allowEdgeOverflow" : false});
        }
        {
            var Q0;
            Q0=makeQuery(id+"F2.opExtrude","CAP_FACE",FACE,{"disambiguationData":[OSD([sQuery(id+"F0.wireOp",EDGE,"E12"),sQuery(id+"F0.wireOp",EDGE,"E13"),sQuery(id+"F0.wireOp",EDGE,"E14"),sQuery(id+"F0.wireOp",EDGE,"E15"),sQuery(id+"F0.wireOp",EDGE,"E17.filletArc"),sQuery(id+"F0.wireOp",EDGE,"E18.filletArc"),sQuery(id+"F0.wireOp",EDGE,"E19.filletArc"),sQuery(id+"F0.wireOp",EDGE,"E20.filletArc"),sQuery(id+"F0.wireOp",EDGE,"E25.0"),sQuery(id+"F0.wireOp",EDGE,"E25.1"),sQuery(id+"F0.wireOp",EDGE,"E25.2"),sQuery(id+"F0.wireOp",EDGE,"E25.3"),sQuery(id+"F0.wireOp",EDGE,"E25.4"),sQuery(id+"F0.wireOp",EDGE,"E25.5"),sQuery(id+"F0.wireOp",EDGE,"E25.6"),sQuery(id+"F0.wireOp",EDGE,"E25.7")])],"isStart":false});
            var sketch = newSketch(context, id + "F16", { "sketchPlane" : qUnion([Q0])});
            skLineSegment(sketch, "E79", {"start": v(0, 90) * mm, "end": v(0, 120) * mm, "construction": true});
            skCircle(sketch, "E80", {"center": v(0, 120) * mm, "radius": 6 * mm});
            skLineSegment(sketch, "E81", {"start": v(-33, 90) * mm, "end": v(-15, 108) * mm});
            skLineSegment(sketch, "E82", {"start": v(-15, 108) * mm, "end": v(-15, 120) * mm});
            skLineSegment(sketch, "E83.MirrorCS", {"start": v(15, 108) * mm, "end": v(15, 120) * mm});
            skLineSegment(sketch, "E84.MirrorCS", {"start": v(33, 90) * mm, "end": v(15, 108) * mm});
            skArc(sketch, "E85", {"start": v(15, 120) * mm, "mid": v(0, 135) * mm, "end": v(-15, 120) * mm});
            skLineSegment(sketch, "E86", {"start": v(-80, 0) * mm, "end": v(80, 0) * mm, "construction": true});
            skLineSegment(sketch, "E87.0", {"start": v(80, -80) * mm, "end": v(80, 80) * mm});
            skArc(sketch, "E87.1", {"start": v(80, 80) * mm, "mid": v(77.07, 87.07) * mm, "end": v(70, 90) * mm});
            skLineSegment(sketch, "E87.2", {"start": v(-70, 90) * mm, "end": v(70, 90) * mm});
            skLineSegment(sketch, "E87.3", {"start": v(-80, -80) * mm, "end": v(-80, 80) * mm});
            skArc(sketch, "E87.4", {"start": v(-70, 90) * mm, "mid": v(-77.07, 87.07) * mm, "end": v(-80, 80) * mm});
            skCircle(sketch, "E87.5", {"center": v(-60, 67.5) * mm, "radius": 4 * mm});
            skCircle(sketch, "E87.6", {"center": v(60, 67.5) * mm, "radius": 4 * mm});
            skArc(sketch, "E87.7", {"start": v(56.15, 48.18) * mm, "mid": v(0, 67.5) * mm, "end": v(-56.15, 48.18) * mm});
            skLineSegment(sketch, "E87.8", {"start": v(60, 40.3) * mm, "end": v(60, -40.3) * mm});
            skLineSegment(sketch, "E87.9", {"start": v(-60, 40.3) * mm, "end": v(-60, -40.3) * mm});
            skArc(sketch, "E87.10", {"start": v(60, 40.3) * mm, "mid": v(58.99, 44.68) * mm, "end": v(56.15, 48.18) * mm});
            skArc(sketch, "E87.11", {"start": v(-56.15, 48.18) * mm, "mid": v(-58.99, 44.68) * mm, "end": v(-60, 40.3) * mm});
            skLineSegment(sketch, "E88.MirrorCS", {"start": v(15, -108) * mm, "end": v(15, -120) * mm});
            skArc(sketch, "E89.MirrorCS", {"start": v(60, -40.3) * mm, "mid": v(58.99, -44.68) * mm, "end": v(56.15, -48.18) * mm});
            skArc(sketch, "E90.MirrorCS", {"start": v(-56.15, -48.18) * mm, "mid": v(-58.99, -44.68) * mm, "end": v(-60, -40.3) * mm});
            skLineSegment(sketch, "E91.MirrorCS", {"start": v(-15, -108) * mm, "end": v(-15, -120) * mm});
            skCircle(sketch, "E92.MirrorC", {"center": v(0, -120) * mm, "radius": 6 * mm});
            skCircle(sketch, "E93.MirrorC", {"center": v(60, -67.5) * mm, "radius": 4 * mm});
            skCircle(sketch, "E94.MirrorC", {"center": v(-60, -67.5) * mm, "radius": 4 * mm});
            skLineSegment(sketch, "E95.MirrorCS", {"start": v(60, -40.3) * mm, "end": v(60, 40.3) * mm});
            skLineSegment(sketch, "E96.MirrorCS", {"start": v(0, -90) * mm, "end": v(0, -120) * mm, "construction": true});
            skLineSegment(sketch, "E97.MirrorCS", {"start": v(80, 80) * mm, "end": v(80, -80) * mm});
            skArc(sketch, "E98.MirrorCS", {"start": v(56.15, -48.18) * mm, "mid": v(0, -67.5) * mm, "end": v(-56.15, -48.18) * mm});
            skLineSegment(sketch, "E99.MirrorCS", {"start": v(-60, -40.3) * mm, "end": v(-60, 40.3) * mm});
            skArc(sketch, "E100.MirrorCS", {"start": v(15, -120) * mm, "mid": v(0, -135) * mm, "end": v(-15, -120) * mm});
            skArc(sketch, "E101.MirrorCS", {"start": v(-70, -90) * mm, "mid": v(-77.07, -87.07) * mm, "end": v(-80, -80) * mm});
            skLineSegment(sketch, "E102.MirrorCS", {"start": v(-33, -90) * mm, "end": v(-15, -108) * mm});
            skArc(sketch, "E103.MirrorCS", {"start": v(80, -80) * mm, "mid": v(77.07, -87.07) * mm, "end": v(70, -90) * mm});
            skLineSegment(sketch, "E104.MirrorCS", {"start": v(-80, 80) * mm, "end": v(-80, -80) * mm});
            skLineSegment(sketch, "E105.MirrorCS", {"start": v(-70, -90) * mm, "end": v(70, -90) * mm});
            skLineSegment(sketch, "E106.MirrorCS", {"start": v(33, -90) * mm, "end": v(15, -108) * mm});
            skSolve(sketch);
        }
        {
            var Q0;
            Q0 = qSketchRegion(id + "F16", true);
            var Q1;
            {var subQ0=sQuery(id+"F0.wireOp",EDGE,"E21.filletArc");var subQ1=sQuery(id+"F0.wireOp",EDGE,"E7");var subQ2=sQuery(id+"F0.wireOp",EDGE,"E6");var subQ3=sQuery(id+"F0.wireOp",EDGE,"E5");var subQ4=sQuery(id+"F0.wireOp",EDGE,"E4");var subQ5=sQuery(id+"F0.wireOp",EDGE,"E22.filletArc");var subQ6=sQuery(id+"F0.wireOp",EDGE,"E1.bottom");var subQ7=sQuery(id+"F0.wireOp",EDGE,"E1.right");var subQ8=sQuery(id+"F0.wireOp",EDGE,"E1.top");var subQ9=sQuery(id+"F0.wireOp",EDGE,"E1.left");var subQ10=sQuery(id+"F0.wireOp",EDGE,"E23.filletArc");var subQ11=sQuery(id+"F0.wireOp",EDGE,"E24.filletArc");Q1=makeQuery(id+"F2.boolean.opBoolean","SPLIT",FACE,{"disambiguationData":[TD([makeQuery(id+"F1.opExtrude","SWEPT_FACE",FACE,{"disambiguationData":[OSD([subQ6])]})])],"derivedFrom":makeQuery(id+"F1.opExtrude","CAP_FACE",FACE,{"disambiguationData":[OSD([subQ6,subQ8,subQ9,subQ7,subQ4,subQ3,subQ2,subQ1,subQ0,subQ5,subQ10,subQ11])],"isStart":true})});}
            extrude(context, id + "F17", {"entities" : qUnion([Q0]), "endBound" : BoundingType.UP_TO_SURFACE, "oppositeDirection" : true, "depth" : 25 * mm, "endBoundEntityFace" : qUnion([Q1]), "offsetDistance" : 25 * mm});
        }
    });
